# Revit family: Hager-VOLTA-Flush_mounted-IP30-With_Cover-With_DIN-Hosted-BE-en
name_source: partatom
category: Electrical Equipment
units: mm (PartAtom-declared; Revit-internal decimal feet)

## family parameters
Cut with Voids When Loaded = No
Host = Face
Maintain Annotation Orientation = Yes
Panel Configuration = Two Columns, Circuits Across
Part Type = Panelboard
Room Calculation Point = No
Round Connector Dimension = Use Diameter
Shared = No

## types (8) — shared parameters
BC_MODEL_ID = 1547080
BC_OBJECT_ID = 513463
BC_OBJECT_VERSION = #38
Code hager = ADD-EC000214_EU
EF000003 - Mounting method = Flush-mounted
EF000007 - Colour = White
EF000008 - Width = 348 mm  [stored 1.14173 ft]
EF000024 - UV resistant = No
EF000049 - Depth = 98 mm  [stored 0.321522 ft]
EF000116 - RAL-number = 9010
EF000218 - Built-in depth = 89 mm  [stored 0.291995 ft]
EF000846 - Built-in width = 315 mm
EF001062 - EMC-version = No
EF001134 - DIN-rail = Yes
EF002950 - Width in number of modular spacings = 12
EF004462 - Type of closure = Other
EF005474 - Degree of protection (IP) = IP30
EF006244 - Transparent cover/door = No
EF006306 - With lock = No
EF009212 - Cover model = With notch
EF015777 - Neutral terminal block = No
EF015941 - Signal passing door = No
ETIM class code = EC000214
ETIM class name = Small distribution board
HG000001-Number of columns = 1
HG000002-With door or cover = Yes
HG000003-Range = VOLTA
HG000005-Thickness = 2 mm  [stored 0.00656168 ft]
HG000006-Flush mounted = Yes
HG000009-Double swing door = No
HG000010-Asymmetric doors = No
HG000011-Empty rows from bottom = No
HG000012-Door swing angle = 90.00°
HG000013-Door on the left = No
HG000014-Door on the right = Yes
HG000015-Clearance visibility = Yes
HG000016-Door 3D visibility = Yes
HG000017-Distance between poles = 18 mm  [stored 0.0590551 ft]
HG000060-RAL-number = 9010
HG000099-Onfly Template ID = 507532
HGEF002950-Width in number of modular spacings = 12
Manufacturer = Hager
Name = VOLTA-Flush_mounted-IP30-With_Cover-With_DIN-BE
Name BIM&CO = Electricity
Name hager = ADD_Enclosures_EC000214
Uniformat = Low Tension Service & Dist.
Uniformat code = D501001
zero-valued in all types: Default Elevation, EF001131 - Inner depth, HG000007-Number of empty columns, HG000008-Number of empty rows

## per-type parameters (varying)
| type | BC_METADATA | BC_VARIANT_ID | EF000040 - Height | EF000118 - With mounting plate | EF000266 - Number of rows | EF000332 - Built-in height | EF001088 - Extension possible | EF015776 - Earthing terminal block | HG000004-Manufacturer reference | HGEF000266-Number of rows |
| VOLTA-Flush_mounted_W348_H356_D98_12_Modular_Spacing-VU12LN | {"ObjectGuid":"67b58f6c-9ae2-4049-b128-79a096434ac7","ModelGuid":"35a3b6d8-1bf3-465d-a120-004a3534f856","VariantGuid":"c4b2000e-8690-4240-8a44-75bc01340489","Revision":"#4","VariantName":"VOLTA-Flush_mounted_W348_H356_D98_12_Modular_Spacing-VU12LN"} | 1174082 | 356 mm  [stored 1.16798 ft] | Yes | 1 | 321 mm  [stored 1.05315 ft] | Yes | Yes | VU12LN | 1 |
| VOLTA-Flush_mounted_W348_H356_D98_12_Modular_Spacing-VU12NC | {"ObjectGuid":"67b58f6c-9ae2-4049-b128-79a096434ac7","ModelGuid":"35a3b6d8-1bf3-465d-a120-004a3534f856","VariantGuid":"27633023-2968-4274-8e31-52e379b8fef9","Revision":"#4","VariantName":"VOLTA-Flush_mounted_W348_H356_D98_12_Modular_Spacing-VU12NC"} | 1174083 | 356 mm  [stored 1.16798 ft] | No | 1 | 321 mm  [stored 1.05315 ft] | No | No | VU12NC | 1 |
| VOLTA-Flush_mounted_W348_H505_D98_12_Modular_Spacing-VU24LN | {"ObjectGuid":"67b58f6c-9ae2-4049-b128-79a096434ac7","ModelGuid":"35a3b6d8-1bf3-465d-a120-004a3534f856","VariantGuid":"e640e0ea-a8f6-4f5b-8664-673fbf1d1ee4","Revision":"#4","VariantName":"VOLTA-Flush_mounted_W348_H505_D98_12_Modular_Spacing-VU24LN"} | 1174084 | 505 mm  [stored 1.65682 ft] | Yes | 2 | 470 mm  [stored 1.54199 ft] | Yes | Yes | VU24LN | 2 |
| VOLTA-Flush_mounted_W348_H505_D98_12_Modular_Spacing-VU24NC | {"ObjectGuid":"67b58f6c-9ae2-4049-b128-79a096434ac7","ModelGuid":"35a3b6d8-1bf3-465d-a120-004a3534f856","VariantGuid":"a37819ed-ff77-4b0b-b0c9-1d28e1e5d970","Revision":"#4","VariantName":"VOLTA-Flush_mounted_W348_H505_D98_12_Modular_Spacing-VU24NC"} | 1174085 | 505 mm  [stored 1.65682 ft] | No | 2 | 470 mm  [stored 1.54199 ft] | No | No | VU24NC | 2 |
| VOLTA-Flush_mounted_W348_H630_D98_12_Modular_Spacing-VU36LN | {"ObjectGuid":"67b58f6c-9ae2-4049-b128-79a096434ac7","ModelGuid":"35a3b6d8-1bf3-465d-a120-004a3534f856","VariantGuid":"5d0c8df7-eebe-4e0c-9795-cb234a2d121c","Revision":"#4","VariantName":"VOLTA-Flush_mounted_W348_H630_D98_12_Modular_Spacing-VU36LN"} | 1174086 | 630 mm  [stored 2.06693 ft] | Yes | 3 | 595 mm  [stored 1.9521 ft] | Yes | Yes | VU36LN | 3 |
| VOLTA-Flush_mounted_W348_H630_D98_12_Modular_Spacing-VU36NC | {"ObjectGuid":"67b58f6c-9ae2-4049-b128-79a096434ac7","ModelGuid":"35a3b6d8-1bf3-465d-a120-004a3534f856","VariantGuid":"d57241c1-f85c-4dcb-bd8b-8695d9346783","Revision":"#4","VariantName":"VOLTA-Flush_mounted_W348_H630_D98_12_Modular_Spacing-VU36NC"} | 1174087 | 630 mm  [stored 2.06693 ft] | No | 3 | 595 mm  [stored 1.9521 ft] | No | No | VU36NC | 3 |
| VOLTA-Flush_mounted_W348_H755_D98_12_Modular_Spacing-VU48LN | {"ObjectGuid":"67b58f6c-9ae2-4049-b128-79a096434ac7","ModelGuid":"35a3b6d8-1bf3-465d-a120-004a3534f856","VariantGuid":"359e88f7-6409-4b71-b620-c63fa405521e","Revision":"#4","VariantName":"VOLTA-Flush_mounted_W348_H755_D98_12_Modular_Spacing-VU48LN"} | 1174088 | 755 mm  [stored 2.47703 ft] | Yes | 4 | 720 mm  [stored 2.3622 ft] | Yes | Yes | VU48LN | 4 |
| VOLTA-Flush_mounted_W348_H755_D98_12_Modular_Spacing-VU48NC | {"ObjectGuid":"67b58f6c-9ae2-4049-b128-79a096434ac7","ModelGuid":"35a3b6d8-1bf3-465d-a120-004a3534f856","VariantGuid":"37790bb2-995f-4cfe-9a07-47a00440aef4","Revision":"#4","VariantName":"VOLTA-Flush_mounted_W348_H755_D98_12_Modular_Spacing-VU48NC"} | 1174089 | 755 mm  [stored 2.47703 ft] | No | 4 | 720 mm  [stored 2.3622 ft] | No | No | VU48NC | 4 |

note: column(s) folded — value = type name in every type: Reference

note: [stored X ft] marks values corroborated as IEEE doubles in the binary element streams (Revit-internal decimal feet)

## geometry (parser evidence)
native form markers: Sweep x14
no freeform markers — native parametric forms only
